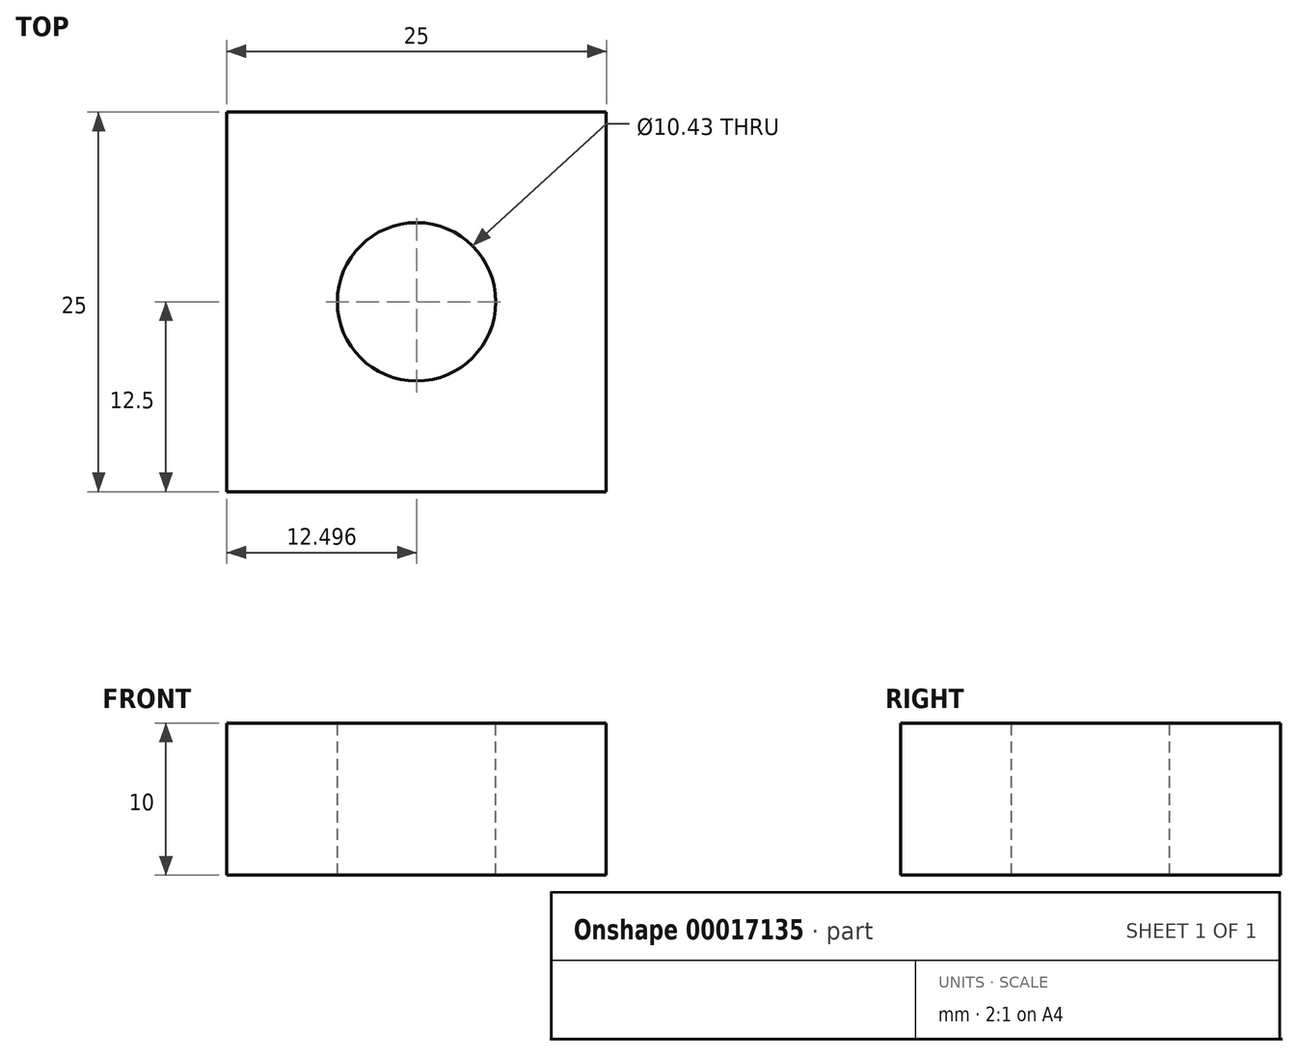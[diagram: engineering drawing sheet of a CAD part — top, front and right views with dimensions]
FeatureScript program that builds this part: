
annotation { "Feature Type Name" : "Feature", "Feature Type Description" : "" }
export const myFeature = defineFeature(function(context is Context, id is Id, definition is map)
    precondition{}
    {
        {
            var Q0;
            Q0=qCreatedBy(makeId("Front.planeOp"),FACE);
            var sketch = newSketch(context, id + "F0", { "sketchPlane" : qUnion([Q0])});
            skLineSegment(sketch, "E0.rect.bottom", {"start": v(-11.84, 16.77) * mm, "end": v(-36.84, 16.77) * mm});
            skLineSegment(sketch, "E0.rect.top", {"start": v(-11.84, 26.77) * mm, "end": v(-36.84, 26.77) * mm});
            skLineSegment(sketch, "E0.rect.left", {"start": v(-11.84, 16.77) * mm, "end": v(-11.84, 26.77) * mm});
            skLineSegment(sketch, "E0.rect.right", {"start": v(-36.84, 16.77) * mm, "end": v(-36.84, 26.77) * mm});
            skPoint(sketch, "E0.rect.middle", {"position": v(-24.34, 21.77) * mm});
            skSolve(sketch);
        }
        {
            var Q0;
            Q0=makeQuery(id+"F0.imprint","IMPRINT",FACE,{"disambiguationData":[TD([[makeQuery(id+"F0.imprint","IMPRINT",EDGE,{"derivedFrom":sQuery(id+"F0.wireOp",EDGE,"E0.rect.bottom")}),-1.0]])]});
            extrude(context, id + "F1", {"entities" : qUnion([Q0]), "depth" : 25 * mm});
        }
        {
            var Q0;
            Q0=makeQuery(id+"F1.opExtrude","SWEPT_FACE",FACE,{"disambiguationData":[OSD([sQuery(id+"F0.wireOp",EDGE,"E0.rect.top")])]});
            var sketch = newSketch(context, id + "F2", { "sketchPlane" : qUnion([Q0])});
            skCircle(sketch, "E1", {"center": v(-24.34, -12.5) * mm, "radius": 5.21 * mm});
            skSolve(sketch);
        }
        {
            var Q0;
            Q0=makeQuery(id+"F2.imprint","IMPRINT",FACE,{"disambiguationData":[TD([[makeQuery(id+"F2.imprint","IMPRINT",EDGE,{"derivedFrom":sQuery(id+"F2.wireOp",EDGE,"E1")}),1.0]])]});
            extrude(context, id + "F3", {"entities" : qUnion([Q0]), "operationType" : NewBodyOperationType.REMOVE, "endBound" : BoundingType.THROUGH_ALL, "oppositeDirection" : true, "depth" : 25 * mm});
        }
    });
